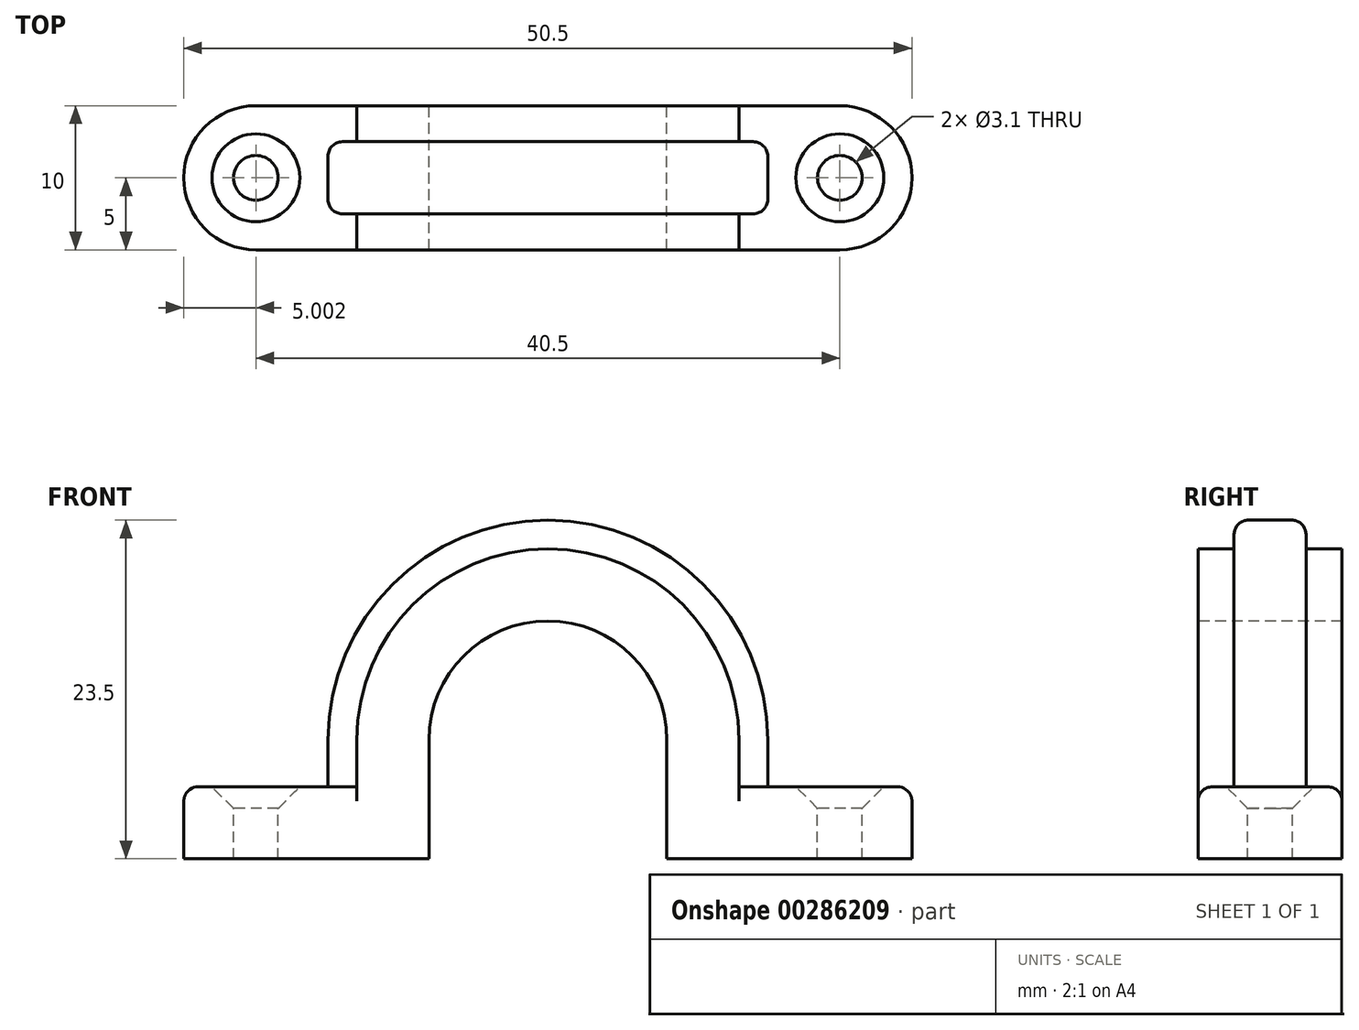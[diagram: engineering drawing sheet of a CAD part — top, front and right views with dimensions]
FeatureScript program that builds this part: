
annotation { "Feature Type Name" : "Feature", "Feature Type Description" : "" }
export const myFeature = defineFeature(function(context is Context, id is Id, definition is map)
    precondition{}
    {
        {
            var Q0;
            Q0=qCreatedBy(makeId("Front.planeOp"),FACE);
            var sketch = newSketch(context, id + "F0", { "sketchPlane" : qUnion([Q0])});
            skLineSegment(sketch, "E0", {"start": v(-7.1, 0) * mm, "end": v(-7.1, 8.25) * mm});
            skLineSegment(sketch, "E1", {"start": v(-7.1, 8.25) * mm, "end": v(-7.1, 16.5) * mm});
            skLineSegment(sketch, "E2", {"start": v(-7.1, 16.5) * mm, "end": v(9.4, 16.5) * mm});
            skLineSegment(sketch, "E3", {"start": v(9.4, 16.5) * mm, "end": v(9.4, 0) * mm});
            skLineSegment(sketch, "E4", {"start": v(9.4, 0) * mm, "end": v(22.4, 0) * mm});
            skLineSegment(sketch, "E5", {"start": v(22.4, 0) * mm, "end": v(22.4, 5) * mm});
            skLineSegment(sketch, "E6", {"start": v(22.4, 5) * mm, "end": v(14.4, 5) * mm});
            skLineSegment(sketch, "E7", {"start": v(14.4, 5) * mm, "end": v(14.4, 21.5) * mm});
            skLineSegment(sketch, "E8", {"start": v(14.4, 21.5) * mm, "end": v(-12.1, 21.5) * mm});
            skLineSegment(sketch, "E9", {"start": v(-12.1, 21.5) * mm, "end": v(-12.1, 5) * mm});
            skLineSegment(sketch, "E10", {"start": v(-12.1, 5) * mm, "end": v(-20.1, 5) * mm});
            skLineSegment(sketch, "E11", {"start": v(-20.1, 5) * mm, "end": v(-20.1, 0) * mm});
            skLineSegment(sketch, "E12", {"start": v(-20.1, 0) * mm, "end": v(-7.1, 0) * mm});
            skLineSegment(sketch, "E13", {"start": v(-14.1, 5) * mm, "end": v(-14.1, 23.5) * mm});
            skLineSegment(sketch, "E14", {"start": v(-14.1, 23.5) * mm, "end": v(16.4, 23.5) * mm});
            skLineSegment(sketch, "E15", {"start": v(16.4, 23.5) * mm, "end": v(16.4, 5) * mm});
            skSolve(sketch);
        }
        {
            var Q0;
            Q0=makeQuery(id+"F0.imprint","IMPRINT",FACE,{"disambiguationData":[TD([[makeQuery(id+"F0.imprint","IMPRINT",EDGE,{"derivedFrom":sQuery(id+"F0.wireOp",EDGE,"E0")}),1.0]])]});
            extrude(context, id + "F1", {"entities" : qUnion([Q0]), "endBound" : BoundingType.SYMMETRIC, "depth" : 10 * mm});
        }
        {
            var Q0;
            {var subQ1=sQuery(id+"F0.wireOp",EDGE,"E7");Q0=makeQuery(id+"F0.imprint","IMPRINT",FACE,{"disambiguationData":[TD([[makeQuery(id+"F0.imprint","IMPRINT",EDGE,{"derivedFrom":subQ1}),-1.0]])]});}
            extrude(context, id + "F2", {"entities" : qUnion([Q0]), "operationType" : NewBodyOperationType.ADD, "endBound" : BoundingType.SYMMETRIC, "depth" : 5 * mm});
        }
        {
            var Q0;
            Q0=makeQuery(id+"F1.opExtrude","SWEPT_EDGE",EDGE,{"disambiguationData":[OSD([sQuery(id+"F0.wireOp",EDGE,"E1"),sQuery(id+"F0.wireOp",EDGE,"E2")])]});
            var Q1;
            Q1=makeQuery(id+"F1.opExtrude","SWEPT_EDGE",EDGE,{"disambiguationData":[OSD([sQuery(id+"F0.wireOp",EDGE,"E2"),sQuery(id+"F0.wireOp",EDGE,"E3")])]});
            fillet(context, id + "F3", {"entities" : qUnion([Q0, Q1]), "radius" : 8.25 * mm, "tangentPropagation" : true, "allowEdgeOverflow" : false});
        }
        {
            var Q0;
            {var subQ0=sQuery(id+"F0.wireOp",EDGE,"E10");var subQ1=sQuery(id+"F0.wireOp",EDGE,"E9");var subQ2=sQuery(id+"F0.wireOp",EDGE,"E8");var subQ3=sQuery(id+"F0.wireOp",EDGE,"E7");var subQ4=sQuery(id+"F0.wireOp",EDGE,"E6");Q0=makeQuery(id+"F2.boolean.opBoolean","SPLIT",EDGE,{"disambiguationData":[TD([makeQuery(id+"F2.opExtrude","CAP_FACE",FACE,{"disambiguationData":[OSD([subQ4,subQ3,subQ2,subQ1,subQ0,sQuery(id+"F0.wireOp",EDGE,"E13"),sQuery(id+"F0.wireOp",EDGE,"E14"),sQuery(id+"F0.wireOp",EDGE,"E15")])],"isStart":false})])],"derivedFrom":makeQuery(id+"F1.opExtrude","SWEPT_EDGE",EDGE,{"disambiguationData":[OSD([subQ3,subQ2])]})});}
            var Q1;
            {var subQ0=sQuery(id+"F0.wireOp",EDGE,"E10");var subQ1=sQuery(id+"F0.wireOp",EDGE,"E9");var subQ2=sQuery(id+"F0.wireOp",EDGE,"E8");var subQ3=sQuery(id+"F0.wireOp",EDGE,"E7");var subQ4=sQuery(id+"F0.wireOp",EDGE,"E6");Q1=makeQuery(id+"F2.boolean.opBoolean","SPLIT",EDGE,{"disambiguationData":[TD([makeQuery(id+"F2.opExtrude","CAP_FACE",FACE,{"disambiguationData":[OSD([subQ4,subQ3,subQ2,subQ1,subQ0,sQuery(id+"F0.wireOp",EDGE,"E13"),sQuery(id+"F0.wireOp",EDGE,"E14"),sQuery(id+"F0.wireOp",EDGE,"E15")])],"isStart":false})])],"derivedFrom":makeQuery(id+"F1.opExtrude","SWEPT_EDGE",EDGE,{"disambiguationData":[OSD([subQ2,subQ1])]})});}
            fillet(context, id + "F4", {"entities" : qUnion([Q0, Q1]), "radius" : (26.5 / 2) * mm, "tangentPropagation" : true, "allowEdgeOverflow" : false});
        }
        {
            var Q0;
            {var subQ0=sQuery(id+"F0.wireOp",EDGE,"E10");var subQ1=sQuery(id+"F0.wireOp",EDGE,"E9");var subQ2=sQuery(id+"F0.wireOp",EDGE,"E8");var subQ3=sQuery(id+"F0.wireOp",EDGE,"E7");var subQ4=sQuery(id+"F0.wireOp",EDGE,"E6");Q0=makeQuery(id+"F2.boolean.opBoolean","SPLIT",EDGE,{"disambiguationData":[TD([makeQuery(id+"F2.opExtrude","CAP_FACE",FACE,{"disambiguationData":[OSD([subQ4,subQ3,subQ2,subQ1,subQ0,sQuery(id+"F0.wireOp",EDGE,"E13"),sQuery(id+"F0.wireOp",EDGE,"E14"),sQuery(id+"F0.wireOp",EDGE,"E15")])],"isStart":true})])],"derivedFrom":makeQuery(id+"F1.opExtrude","SWEPT_EDGE",EDGE,{"disambiguationData":[OSD([subQ3,subQ2])]})});}
            var Q1;
            {var subQ0=sQuery(id+"F0.wireOp",EDGE,"E10");var subQ1=sQuery(id+"F0.wireOp",EDGE,"E9");var subQ2=sQuery(id+"F0.wireOp",EDGE,"E8");var subQ3=sQuery(id+"F0.wireOp",EDGE,"E7");var subQ4=sQuery(id+"F0.wireOp",EDGE,"E6");Q1=makeQuery(id+"F2.boolean.opBoolean","SPLIT",EDGE,{"disambiguationData":[TD([makeQuery(id+"F2.opExtrude","CAP_FACE",FACE,{"disambiguationData":[OSD([subQ4,subQ3,subQ2,subQ1,subQ0,sQuery(id+"F0.wireOp",EDGE,"E13"),sQuery(id+"F0.wireOp",EDGE,"E14"),sQuery(id+"F0.wireOp",EDGE,"E15")])],"isStart":true})])],"derivedFrom":makeQuery(id+"F1.opExtrude","SWEPT_EDGE",EDGE,{"disambiguationData":[OSD([subQ2,subQ1])]})});}
            fillet(context, id + "F5", {"entities" : qUnion([Q0, Q1]), "radius" : (26.5 / 2) * mm, "tangentPropagation" : true, "allowEdgeOverflow" : false});
        }
        {
            var Q0;
            Q0=makeQuery(id+"F2.opExtrude","SWEPT_EDGE",EDGE,{"disambiguationData":[OSD([sQuery(id+"F0.wireOp",EDGE,"E14"),sQuery(id+"F0.wireOp",EDGE,"E15")])]});
            var Q1;
            Q1=makeQuery(id+"F2.opExtrude","SWEPT_EDGE",EDGE,{"disambiguationData":[OSD([sQuery(id+"F0.wireOp",EDGE,"E13"),sQuery(id+"F0.wireOp",EDGE,"E14")])]});
            fillet(context, id + "F6", {"entities" : qUnion([Q0, Q1]), "radius" : (30.5 / 2) * mm, "tangentPropagation" : true, "allowEdgeOverflow" : false});
        }
        {
            var Q0;
            Q0=makeQuery(id+"F1.opExtrude","SWEPT_FACE",FACE,{"disambiguationData":[OSD([sQuery(id+"F0.wireOp",EDGE,"E5")])]});
            extrude(context, id + "F7", {"entities" : qUnion([Q0]), "operationType" : NewBodyOperationType.ADD, "depth" : 4 * mm});
        }
        {
            var Q0;
            Q0=makeQuery(id+"F1.opExtrude","SWEPT_FACE",FACE,{"disambiguationData":[OSD([sQuery(id+"F0.wireOp",EDGE,"E11")])]});
            extrude(context, id + "F8", {"entities" : qUnion([Q0]), "operationType" : NewBodyOperationType.ADD, "depth" : 4 * mm});
        }
        {
            var Q0;
            {var subQ0=sQuery(id+"F0.wireOp",EDGE,"E5");Q0=makeQuery(id+"F7.opExtrude","CAP_EDGE",EDGE,{"disambiguationData":[OSD([subQ0]),TDD([makeQuery(id+"F1.opExtrude","CAP_EDGE",EDGE,{"disambiguationData":[OSD([subQ0])],"isStart":false})])],"isStart":false});}
            var Q1;
            {var subQ0=sQuery(id+"F0.wireOp",EDGE,"E5");Q1=makeQuery(id+"F7.opExtrude","CAP_EDGE",EDGE,{"disambiguationData":[OSD([subQ0]),TDD([makeQuery(id+"F1.opExtrude","CAP_EDGE",EDGE,{"disambiguationData":[OSD([subQ0])],"isStart":true})])],"isStart":false});}
            var Q2;
            {var subQ0=sQuery(id+"F0.wireOp",EDGE,"E11");Q2=makeQuery(id+"F8.opExtrude","CAP_EDGE",EDGE,{"disambiguationData":[OSD([subQ0]),TDD([makeQuery(id+"F1.opExtrude","CAP_EDGE",EDGE,{"disambiguationData":[OSD([subQ0])],"isStart":false})])],"isStart":false});}
            var Q3;
            {var subQ0=sQuery(id+"F0.wireOp",EDGE,"E11");Q3=makeQuery(id+"F8.opExtrude","CAP_EDGE",EDGE,{"disambiguationData":[OSD([subQ0]),TDD([makeQuery(id+"F1.opExtrude","CAP_EDGE",EDGE,{"disambiguationData":[OSD([subQ0])],"isStart":true})])],"isStart":false});}
            fillet(context, id + "F9", {"entities" : qUnion([Q0, Q1, Q2, Q3]), "radius" : 5 * mm, "tangentPropagation" : true, "allowEdgeOverflow" : false});
        }
        {
            var Q0;
            {var subQ0=sQuery(id+"F0.wireOp",EDGE,"E10");Q0=makeQuery(id+"F8.boolean.opBoolean","MERGE",FACE,{"derivedFrom":[makeQuery(id+"F1.opExtrude","SWEPT_FACE",FACE,{"disambiguationData":[OSD([subQ0])]}),makeQuery(id+"F8.opExtrude","SWEPT_FACE",FACE,{"disambiguationData":[OSD([subQ0,sQuery(id+"F0.wireOp",EDGE,"E11")])]})]});}
            var sketch = newSketch(context, id + "F10", { "sketchPlane" : qUnion([Q0])});
            skPoint(sketch, "E16", {"position": v(-19.1, 0) * mm});
            skSolve(sketch);
        }
        {
            var Q0;
            Q0=sQuery(id+"F10.wireOp",VERTEX,"E16");
            var Q1;
            Q1=makeQuery(id+"F1.opExtrude","SWEPT_BODY",BODY,{"disambiguationData":[OSD([sQuery(id+"F0.wireOp",EDGE,"E0"),sQuery(id+"F0.wireOp",EDGE,"E1"),sQuery(id+"F0.wireOp",EDGE,"E2"),sQuery(id+"F0.wireOp",EDGE,"E3"),sQuery(id+"F0.wireOp",EDGE,"E4"),sQuery(id+"F0.wireOp",EDGE,"E5"),sQuery(id+"F0.wireOp",EDGE,"E6"),sQuery(id+"F0.wireOp",EDGE,"E7"),sQuery(id+"F0.wireOp",EDGE,"E8"),sQuery(id+"F0.wireOp",EDGE,"E9"),sQuery(id+"F0.wireOp",EDGE,"E10"),sQuery(id+"F0.wireOp",EDGE,"E11"),sQuery(id+"F0.wireOp",EDGE,"E12")])]});
            hole(context, id + "F11", {"style" : HoleStyle.C_SINK, "endStyle" : HoleEndStyle.THROUGH, "holeDiameter" : 3.1 * mm, "cSinkDiameter" : 6.1 * mm, "cSinkAngle" : 90 * degree, "tappedDepth" : 12 * mm, "tapClearance" : 3, "locations" : qUnion([Q0]), "scope" : qUnion([Q1])});
        }
        {
            var Q0;
            {var subQ0=sQuery(id+"F0.wireOp",EDGE,"E6");Q0=makeQuery(id+"F7.boolean.opBoolean","MERGE",FACE,{"derivedFrom":[makeQuery(id+"F1.opExtrude","SWEPT_FACE",FACE,{"disambiguationData":[OSD([subQ0])]}),makeQuery(id+"F7.opExtrude","SWEPT_FACE",FACE,{"disambiguationData":[OSD([sQuery(id+"F0.wireOp",EDGE,"E5"),subQ0])]})]});}
            var sketch = newSketch(context, id + "F12", { "sketchPlane" : qUnion([Q0])});
            skPoint(sketch, "E17", {"position": v(21.4, 0) * mm});
            skSolve(sketch);
        }
        {
            var Q0;
            Q0=sQuery(id+"F12.wireOp",VERTEX,"E17");
            var Q1;
            Q1=makeQuery(id+"F1.opExtrude","SWEPT_BODY",BODY,{"disambiguationData":[OSD([sQuery(id+"F0.wireOp",EDGE,"E0"),sQuery(id+"F0.wireOp",EDGE,"E1"),sQuery(id+"F0.wireOp",EDGE,"E2"),sQuery(id+"F0.wireOp",EDGE,"E3"),sQuery(id+"F0.wireOp",EDGE,"E4"),sQuery(id+"F0.wireOp",EDGE,"E5"),sQuery(id+"F0.wireOp",EDGE,"E6"),sQuery(id+"F0.wireOp",EDGE,"E7"),sQuery(id+"F0.wireOp",EDGE,"E8"),sQuery(id+"F0.wireOp",EDGE,"E9"),sQuery(id+"F0.wireOp",EDGE,"E10"),sQuery(id+"F0.wireOp",EDGE,"E11"),sQuery(id+"F0.wireOp",EDGE,"E12")])]});
            hole(context, id + "F13", {"style" : HoleStyle.C_SINK, "endStyle" : HoleEndStyle.THROUGH, "holeDiameter" : 3.1 * mm, "cSinkDiameter" : 6.1 * mm, "cSinkAngle" : 90 * degree, "tappedDepth" : 12 * mm, "tapClearance" : 3, "locations" : qUnion([Q0]), "scope" : qUnion([Q1])});
        }
        {
            var Q0;
            {var subQ0=sQuery(id+"F0.wireOp",EDGE,"E10");var subQ1=sQuery(id+"F0.wireOp",EDGE,"E9");var subQ2=sQuery(id+"F0.wireOp",EDGE,"E8");var subQ3=sQuery(id+"F0.wireOp",EDGE,"E7");var subQ4=sQuery(id+"F0.wireOp",EDGE,"E6");var subQ5=makeQuery(id+"F1.opExtrude","CAP_FACE",FACE,{"disambiguationData":[OSD([sQuery(id+"F0.wireOp",EDGE,"E0"),sQuery(id+"F0.wireOp",EDGE,"E1"),sQuery(id+"F0.wireOp",EDGE,"E2"),sQuery(id+"F0.wireOp",EDGE,"E3"),sQuery(id+"F0.wireOp",EDGE,"E4"),sQuery(id+"F0.wireOp",EDGE,"E5"),subQ4,subQ3,subQ2,subQ1,subQ0,sQuery(id+"F0.wireOp",EDGE,"E11"),sQuery(id+"F0.wireOp",EDGE,"E12")])],"isStart":false});Q0=makeQuery(id+"F4.opFillet","BLEND_EDGE",EDGE,{"blendedFrom":[makeQuery(id+"F2.boolean.opBoolean","SPLIT",EDGE,{"disambiguationData":[TD([makeQuery(id+"F2.opExtrude","CAP_FACE",FACE,{"disambiguationData":[OSD([subQ4,subQ3,subQ2,subQ1,subQ0,sQuery(id+"F0.wireOp",EDGE,"E13"),sQuery(id+"F0.wireOp",EDGE,"E14"),sQuery(id+"F0.wireOp",EDGE,"E15")])],"isStart":false})])],"derivedFrom":makeQuery(id+"F1.opExtrude","SWEPT_EDGE",EDGE,{"disambiguationData":[OSD([subQ2,subQ1])]})}),subQ5],"blendedInto":[subQ5]});}
            var Q1;
            {var subQ0=sQuery(id+"F0.wireOp",EDGE,"E14");var subQ1=sQuery(id+"F0.wireOp",EDGE,"E13");Q1=makeQuery(id+"F6.opFillet","BLEND_EDGE",EDGE,{"blendedFrom":[makeQuery(id+"F2.opExtrude","SWEPT_EDGE",EDGE,{"disambiguationData":[OSD([subQ1,subQ0])]}),makeQuery(id+"F2.opExtrude","CAP_FACE",FACE,{"disambiguationData":[OSD([sQuery(id+"F0.wireOp",EDGE,"E6"),sQuery(id+"F0.wireOp",EDGE,"E7"),sQuery(id+"F0.wireOp",EDGE,"E8"),sQuery(id+"F0.wireOp",EDGE,"E9"),sQuery(id+"F0.wireOp",EDGE,"E10"),subQ1,subQ0,sQuery(id+"F0.wireOp",EDGE,"E15")])],"isStart":false})],"blendedInto":[makeQuery(id+"F2.opExtrude","CAP_FACE",FACE,{"disambiguationData":[OSD([sQuery(id+"F0.wireOp",EDGE,"E6"),sQuery(id+"F0.wireOp",EDGE,"E7"),sQuery(id+"F0.wireOp",EDGE,"E8"),sQuery(id+"F0.wireOp",EDGE,"E9"),sQuery(id+"F0.wireOp",EDGE,"E10"),subQ1,subQ0,sQuery(id+"F0.wireOp",EDGE,"E15")])],"isStart":false})]});}
            var Q2;
            {var subQ0=sQuery(id+"F0.wireOp",EDGE,"E10");var subQ1=sQuery(id+"F0.wireOp",EDGE,"E9");var subQ2=sQuery(id+"F0.wireOp",EDGE,"E8");var subQ3=sQuery(id+"F0.wireOp",EDGE,"E7");var subQ4=sQuery(id+"F0.wireOp",EDGE,"E6");var subQ5=makeQuery(id+"F1.opExtrude","CAP_FACE",FACE,{"disambiguationData":[OSD([sQuery(id+"F0.wireOp",EDGE,"E0"),sQuery(id+"F0.wireOp",EDGE,"E1"),sQuery(id+"F0.wireOp",EDGE,"E2"),sQuery(id+"F0.wireOp",EDGE,"E3"),sQuery(id+"F0.wireOp",EDGE,"E4"),sQuery(id+"F0.wireOp",EDGE,"E5"),subQ4,subQ3,subQ2,subQ1,subQ0,sQuery(id+"F0.wireOp",EDGE,"E11"),sQuery(id+"F0.wireOp",EDGE,"E12")])],"isStart":true});Q2=makeQuery(id+"F5.opFillet","BLEND_EDGE",EDGE,{"blendedFrom":[makeQuery(id+"F2.boolean.opBoolean","SPLIT",EDGE,{"disambiguationData":[TD([makeQuery(id+"F2.opExtrude","CAP_FACE",FACE,{"disambiguationData":[OSD([subQ4,subQ3,subQ2,subQ1,subQ0,sQuery(id+"F0.wireOp",EDGE,"E13"),sQuery(id+"F0.wireOp",EDGE,"E14"),sQuery(id+"F0.wireOp",EDGE,"E15")])],"isStart":true})])],"derivedFrom":makeQuery(id+"F1.opExtrude","SWEPT_EDGE",EDGE,{"disambiguationData":[OSD([subQ2,subQ1])]})}),subQ5],"blendedInto":[subQ5]});}
            var Q3;
            {var subQ0=sQuery(id+"F0.wireOp",EDGE,"E14");var subQ1=sQuery(id+"F0.wireOp",EDGE,"E13");Q3=makeQuery(id+"F6.opFillet","BLEND_EDGE",EDGE,{"blendedFrom":[makeQuery(id+"F2.opExtrude","SWEPT_EDGE",EDGE,{"disambiguationData":[OSD([subQ1,subQ0])]}),makeQuery(id+"F2.opExtrude","CAP_FACE",FACE,{"disambiguationData":[OSD([sQuery(id+"F0.wireOp",EDGE,"E6"),sQuery(id+"F0.wireOp",EDGE,"E7"),sQuery(id+"F0.wireOp",EDGE,"E8"),sQuery(id+"F0.wireOp",EDGE,"E9"),sQuery(id+"F0.wireOp",EDGE,"E10"),subQ1,subQ0,sQuery(id+"F0.wireOp",EDGE,"E15")])],"isStart":true})],"blendedInto":[makeQuery(id+"F2.opExtrude","CAP_FACE",FACE,{"disambiguationData":[OSD([sQuery(id+"F0.wireOp",EDGE,"E6"),sQuery(id+"F0.wireOp",EDGE,"E7"),sQuery(id+"F0.wireOp",EDGE,"E8"),sQuery(id+"F0.wireOp",EDGE,"E9"),sQuery(id+"F0.wireOp",EDGE,"E10"),subQ1,subQ0,sQuery(id+"F0.wireOp",EDGE,"E15")])],"isStart":true})]});}
            var Q4;
            {var subQ0=sQuery(id+"F0.wireOp",EDGE,"E6");var subQ1=sQuery(id+"F0.wireOp",EDGE,"E5");Q4=makeQuery(id+"F7.boolean.opBoolean","MERGE",EDGE,{"derivedFrom":[makeQuery(id+"F1.opExtrude","CAP_EDGE",EDGE,{"disambiguationData":[OSD([subQ0])],"isStart":true}),makeQuery(id+"F7.opExtrude","SWEPT_EDGE",EDGE,{"disambiguationData":[OSD([subQ1,subQ0]),TDD([makeQuery(id+"F1.opExtrude","CAP_VERTEX",VERTEX,{"disambiguationData":[OSD([subQ1,subQ0])],"isStart":true})])]})]});}
            var Q5;
            {var subQ0=sQuery(id+"F0.wireOp",EDGE,"E11");var subQ1=sQuery(id+"F0.wireOp",EDGE,"E10");Q5=makeQuery(id+"F8.boolean.opBoolean","MERGE",EDGE,{"derivedFrom":[makeQuery(id+"F1.opExtrude","CAP_EDGE",EDGE,{"disambiguationData":[OSD([subQ1])],"isStart":true}),makeQuery(id+"F8.opExtrude","SWEPT_EDGE",EDGE,{"disambiguationData":[OSD([subQ1,subQ0]),TDD([makeQuery(id+"F1.opExtrude","CAP_VERTEX",VERTEX,{"disambiguationData":[OSD([subQ1,subQ0])],"isStart":true})])]})]});}
            fillet(context, id + "F14", {"entities" : qUnion([Q0, Q1, Q2, Q3, Q4, Q5]), "radius" : 1 * mm, "tangentPropagation" : true, "allowEdgeOverflow" : false});
        }
    });
